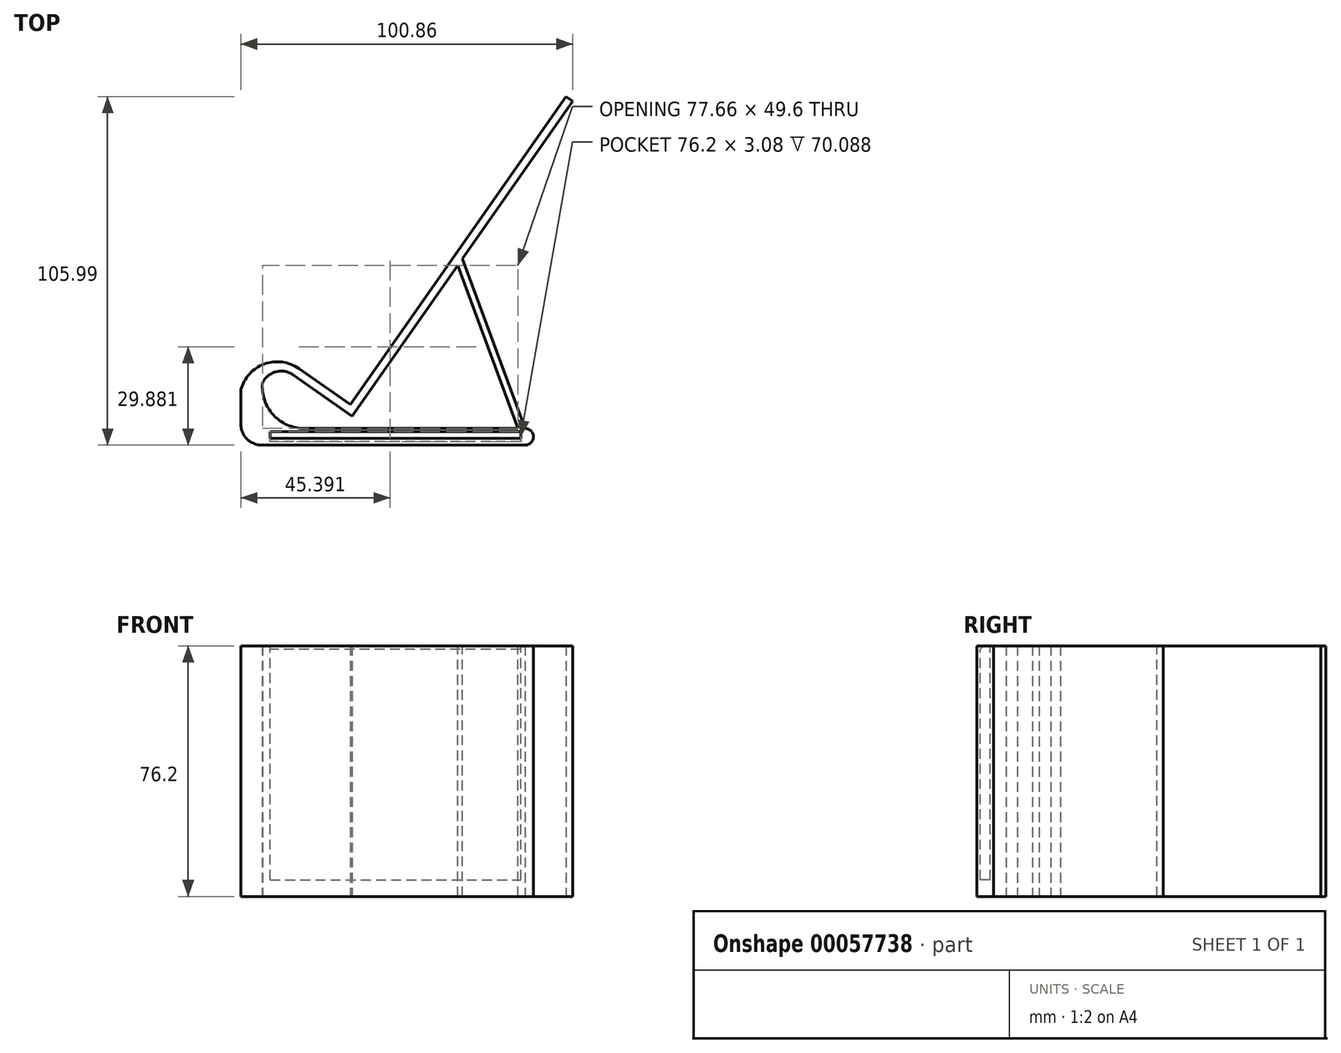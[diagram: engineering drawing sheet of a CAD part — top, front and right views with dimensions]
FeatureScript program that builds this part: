
annotation { "Feature Type Name" : "Feature", "Feature Type Description" : "" }
export const myFeature = defineFeature(function(context is Context, id is Id, definition is map)
    precondition{}
    {
        {
            var Q0;
            Q0=qCreatedBy(makeId("Top.planeOp"),FACE);
            var sketch = newSketch(context, id + "F0", { "sketchPlane" : qUnion([Q0])});
            skLineSegment(sketch, "E0.bottom", {"start": v(-2.54, 0) * mm, "end": v(-71.12, 0) * mm});
            skLineSegment(sketch, "E1", {"start": v(-71.42, 23.39) * mm, "end": v(-71.28, 23.29) * mm});
            skLineSegment(sketch, "E2", {"start": v(-11.74, 101.32) * mm, "end": v(-11.74, 101.32) * mm});
            skLineSegment(sketch, "E3", {"start": v(-70.8, 19.85) * mm, "end": v(-72.96, 21.36) * mm});
            skLineSegment(sketch, "E4", {"start": v(-2.54, 5.08) * mm, "end": v(-69.68, 5.08) * mm});
            skPoint(sketch, "E5.visualSharp", {"position": v(-88.9, 0) * mm});
            skPoint(sketch, "E6.visualSharp", {"position": v(-71.12, 5.08) * mm});
            skArc(sketch, "E6.filletArc", {"start": v(-82.33, 18.9) * mm, "mid": v(-79.04, 9.2) * mm, "end": v(-69.68, 5.08) * mm});
            skLineSegment(sketch, "E7", {"start": v(0, 2.54) * mm, "end": v(0, 2.54) * mm});
            skPoint(sketch, "E8.orphan", {"position": v(-0.2, 5.08) * mm});
            skPoint(sketch, "E9.visualSharp", {"position": v(0, 5.08) * mm});
            skArc(sketch, "E9.filletArc", {"start": v(0, 2.54) * mm, "mid": v(-0.74, 4.34) * mm, "end": v(-2.54, 5.08) * mm});
            skPoint(sketch, "E10.visualSharp", {"position": v(0, 0) * mm});
            skArc(sketch, "E10.filletArc", {"start": v(-2.54, 0) * mm, "mid": v(-0.74, 0.74) * mm, "end": v(0, 2.54) * mm});
            skPoint(sketch, "E11.visualSharp", {"position": v(-16.85, 101.32) * mm});
            skPoint(sketch, "E12.visualSharp", {"position": v(-13.75, 101.32) * mm});
            skPoint(sketch, "E13.visualSharp", {"position": v(-83.53, 28.76) * mm});
            skArc(sketch, "E13.filletArc", {"start": v(-72.96, 21.36) * mm, "mid": v(-78.21, 22.3) * mm, "end": v(-82.33, 18.9) * mm});
            skPoint(sketch, "E14.visualSharp", {"position": v(-92.23, 37.95) * mm});
            skArc(sketch, "E14.filletArc", {"start": v(-71.28, 23.29) * mm, "mid": v(-81.75, 24.66) * mm, "end": v(-88.88, 16.87) * mm});
            skLineSegment(sketch, "E15", {"start": v(-88.88, 16.87) * mm, "end": v(-88.9, 6.36) * mm});
            skLineSegment(sketch, "E16", {"start": v(-82.54, 0) * mm, "end": v(-71.12, 0) * mm});
            skArc(sketch, "E17.filletArc", {"start": v(-88.9, 6.36) * mm, "mid": v(-87.03, 1.86) * mm, "end": v(-82.54, 0) * mm});
            skLineSegment(sketch, "E18", {"start": v(-71.28, 23.29) * mm, "end": v(-55.67, 12.36) * mm});
            skLineSegment(sketch, "E19", {"start": v(-70.8, 19.85) * mm, "end": v(-55.05, 8.82) * mm});
            skLineSegment(sketch, "E20", {"start": v(-55.05, 8.82) * mm, "end": v(11.97, 104.53) * mm});
            skLineSegment(sketch, "E21", {"start": v(11.97, 104.53) * mm, "end": v(9.89, 105.99) * mm});
            skLineSegment(sketch, "E22", {"start": v(9.89, 105.99) * mm, "end": v(-55.67, 12.36) * mm});
            skSolve(sketch);
        }
        {
            var Q0;
            Q0=makeQuery(id+"F0.imprint","IMPRINT",FACE,{"disambiguationData":[TD([[makeQuery(id+"F0.imprint","IMPRINT",EDGE,{"derivedFrom":sQuery(id+"F0.wireOp",EDGE,"E0.bottom")}),-1.0]])]});
            extrude(context, id + "F1", {"entities" : qUnion([Q0]), "depth" : 76.2 * mm});
        }
        {
            var Q0;
            Q0=makeQuery(id+"F1.opExtrude","CAP_FACE",FACE,{"disambiguationData":[OSD([sQuery(id+"F0.wireOp",EDGE,"E0.bottom"),sQuery(id+"F0.wireOp",EDGE,"E1"),sQuery(id+"F0.wireOp",EDGE,"VzQHVXDK-ADtm-Tlph-Cnhg-XIErh8iYJDgg"),sQuery(id+"F0.wireOp",EDGE,"29hdyGJE-8E7G-NRjQ-NpL0-hCzWqXYodk6g"),sQuery(id+"F0.wireOp",EDGE,"E3"),sQuery(id+"F0.wireOp",EDGE,"E4"),sQuery(id+"F0.wireOp",EDGE,"E5.filletArc"),sQuery(id+"F0.wireOp",EDGE,"E6.filletArc"),sQuery(id+"F0.wireOp",EDGE,"E9.filletArc"),sQuery(id+"F0.wireOp",EDGE,"E10.filletArc"),sQuery(id+"F0.wireOp",EDGE,"E13.filletArc"),sQuery(id+"F0.wireOp",EDGE,"E14.filletArc"),sQuery(id+"F0.wireOp",EDGE,"mFCUCqz3-Yqys-O9HQ-v6NA-gGyAUWKn8dcj")])],"isStart":false});
            var sketch = newSketch(context, id + "F2", { "sketchPlane" : qUnion([Q0])});
            skLineSegment(sketch, "E23.bottom", {"start": v(-80, 4.08) * mm, "end": v(-3.8, 4.08) * mm});
            skLineSegment(sketch, "E23.top", {"start": v(-80, 1) * mm, "end": v(-3.8, 1) * mm});
            skLineSegment(sketch, "E23.left", {"start": v(-80, 4.08) * mm, "end": v(-80, 1) * mm});
            skLineSegment(sketch, "E23.right", {"start": v(-3.8, 4.08) * mm, "end": v(-3.8, 1) * mm});
            skSolve(sketch);
        }
        {
            var Q0;
            Q0=makeQuery(id+"F2.imprint","IMPRINT",FACE,{"disambiguationData":[TD([[makeQuery(id+"F2.imprint","IMPRINT",EDGE,{"derivedFrom":sQuery(id+"F2.wireOp",EDGE,"E23.bottom")}),-1.0]])]});
            extrude(context, id + "F3", {"entities" : qUnion([Q0]), "operationType" : NewBodyOperationType.REMOVE, "oppositeDirection" : true, "depth" : 71.12 * mm});
        }
        {
            var Q0;
            Q0=qCreatedBy(makeId("Front.planeOp"),FACE);
            var sketch = newSketch(context, id + "F4", { "sketchPlane" : qUnion([Q0])});
            skLineSegment(sketch, "E24.bottom", {"start": v(-3.8, 76.2) * mm, "end": v(-80, 76.2) * mm});
            skLineSegment(sketch, "E24.top", {"start": v(-3.8, 73.66) * mm, "end": v(-80, 73.66) * mm});
            skLineSegment(sketch, "E24.left", {"start": v(-3.8, 76.2) * mm, "end": v(-3.8, 73.66) * mm});
            skLineSegment(sketch, "E24.right", {"start": v(-80, 76.2) * mm, "end": v(-80, 73.66) * mm});
            skSolve(sketch);
        }
        {
            var Q0;
            Q0=makeQuery(id+"F4.imprint","IMPRINT",FACE,{"disambiguationData":[TD([[makeQuery(id+"F4.imprint","IMPRINT",EDGE,{"derivedFrom":sQuery(id+"F4.wireOp",EDGE,"E24.bottom")}),1.0]])]});
            extrude(context, id + "F5", {"entities" : qUnion([Q0]), "operationType" : NewBodyOperationType.ADD, "oppositeDirection" : true, "depth" : 2.03 * mm});
        }
        {
            var Q0;
            Q0=makeQuery(id+"F5.opExtrude","CAP_EDGE",EDGE,{"disambiguationData":[OSD([sQuery(id+"F4.wireOp",EDGE,"E24.top")])],"isStart":false});
            chamfer(context, id + "F6", {"entities" : qUnion([Q0]), "width" : 2.54 * mm, "tangentPropagation" : true});
        }
        {
            var Q0;
            Q0=makeQuery(id+"F5.boolean.opBoolean","MERGE",FACE,{"derivedFrom":[makeQuery(id+"F1.opExtrude","CAP_FACE",FACE,{"disambiguationData":[OSD([sQuery(id+"F0.wireOp",EDGE,"E0.bottom"),sQuery(id+"F0.wireOp",EDGE,"E1"),sQuery(id+"F0.wireOp",EDGE,"VzQHVXDK-ADtm-Tlph-Cnhg-XIErh8iYJDgg"),sQuery(id+"F0.wireOp",EDGE,"29hdyGJE-8E7G-NRjQ-NpL0-hCzWqXYodk6g"),sQuery(id+"F0.wireOp",EDGE,"E3"),sQuery(id+"F0.wireOp",EDGE,"E4"),sQuery(id+"F0.wireOp",EDGE,"E6.filletArc"),sQuery(id+"F0.wireOp",EDGE,"E9.filletArc"),sQuery(id+"F0.wireOp",EDGE,"E10.filletArc"),sQuery(id+"F0.wireOp",EDGE,"E13.filletArc"),sQuery(id+"F0.wireOp",EDGE,"E14.filletArc"),sQuery(id+"F0.wireOp",EDGE,"mFCUCqz3-Yqys-O9HQ-v6NA-gGyAUWKn8dcj"),sQuery(id+"F0.wireOp",EDGE,"E15"),sQuery(id+"F0.wireOp",EDGE,"E16"),sQuery(id+"F0.wireOp",EDGE,"E17.filletArc")])],"isStart":false}),makeQuery(id+"F5.opExtrude","SWEPT_FACE",FACE,{"disambiguationData":[OSD([sQuery(id+"F4.wireOp",EDGE,"E24.bottom")])]})]});
            var sketch = newSketch(context, id + "F7", { "sketchPlane" : qUnion([Q0])});
            skLineSegment(sketch, "E25", {"start": v(-2.54, 5.08) * mm, "end": v(-21.54, 56.68) * mm});
            skLineSegment(sketch, "E26", {"start": v(-21.54, 56.68) * mm, "end": v(-22.94, 54.68) * mm});
            skLineSegment(sketch, "E27", {"start": v(-22.94, 54.68) * mm, "end": v(-4.67, 5.08) * mm});
            skLineSegment(sketch, "E28", {"start": v(-4.67, 5.08) * mm, "end": v(-2.54, 5.08) * mm});
            skSolve(sketch);
        }
        {
            var Q0;
            Q0=makeQuery(id+"F7.imprint","IMPRINT",FACE,{"disambiguationData":[TD([[makeQuery(id+"F7.imprint","IMPRINT",EDGE,{"derivedFrom":sQuery(id+"F7.wireOp",EDGE,"E25")}),1.0]])]});
            extrude(context, id + "F8", {"entities" : qUnion([Q0]), "operationType" : NewBodyOperationType.ADD, "oppositeDirection" : true, "depth" : 76.2 * mm});
        }
    });
